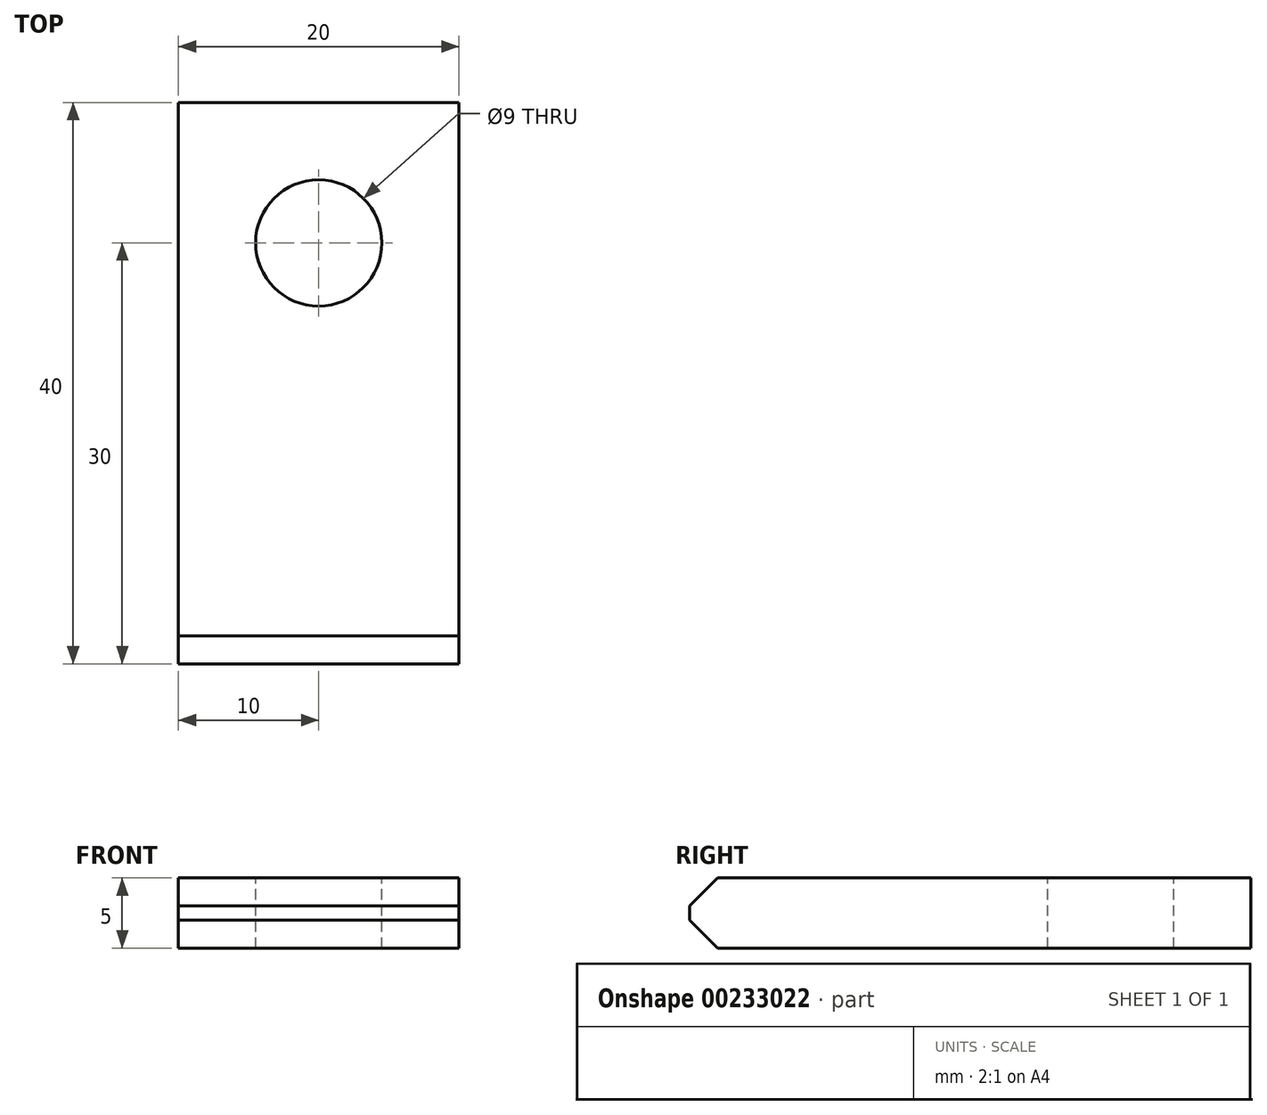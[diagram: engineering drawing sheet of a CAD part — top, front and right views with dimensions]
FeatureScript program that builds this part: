
annotation { "Feature Type Name" : "Feature", "Feature Type Description" : "" }
export const myFeature = defineFeature(function(context is Context, id is Id, definition is map)
    precondition{}
    {
        {
            var Q0;
            Q0=qCreatedBy(makeId("Front.planeOp"),FACE);
            var sketch = newSketch(context, id + "F0", { "sketchPlane" : qUnion([Q0])});
            skLineSegment(sketch, "E0.bottom", {"start": v(10, 2.5) * mm, "end": v(-10, 2.5) * mm});
            skLineSegment(sketch, "E0.top", {"start": v(10, -2.5) * mm, "end": v(-10, -2.5) * mm});
            skLineSegment(sketch, "E0.left", {"start": v(10, 2.5) * mm, "end": v(10, -2.5) * mm});
            skLineSegment(sketch, "E0.right", {"start": v(-10, 2.5) * mm, "end": v(-10, -2.5) * mm});
            skPoint(sketch, "E0.middle", {"position": v(0, 0) * mm});
            skSolve(sketch);
        }
        {
            var Q0;
            Q0=makeQuery(id+"F0.imprint","IMPRINT",FACE,{"disambiguationData":[TD([[makeQuery(id+"F0.imprint","IMPRINT",EDGE,{"derivedFrom":sQuery(id+"F0.wireOp",EDGE,"E0.bottom")}),1.0]])]});
            extrude(context, id + "F1", {"entities" : qUnion([Q0]), "depth" : 40 * mm});
        }
        {
            var Q0;
            Q0=makeQuery(id+"F1.opExtrude","SWEPT_FACE",FACE,{"disambiguationData":[OSD([sQuery(id+"F0.wireOp",EDGE,"E0.bottom")])]});
            var sketch = newSketch(context, id + "F2", { "sketchPlane" : qUnion([Q0])});
            skCircle(sketch, "E1", {"center": v(0, -10) * mm, "radius": 8 * mm, "construction": true});
            skSolve(sketch);
        }
        {
            var Q0;
            Q0=sQuery(id+"F2.wireOp",VERTEX,"E1.center");
            var Q1;
            Q1=makeQuery(id+"F1.opExtrude","SWEPT_BODY",BODY,{"disambiguationData":[OSD([sQuery(id+"F0.wireOp",EDGE,"E0.bottom"),sQuery(id+"F0.wireOp",EDGE,"E0.top"),sQuery(id+"F0.wireOp",EDGE,"E0.left"),sQuery(id+"F0.wireOp",EDGE,"E0.right")])]});
            hole(context, id + "F3", {"style" : HoleStyle.SIMPLE, "endStyle" : HoleEndStyle.THROUGH, "holeDiameter" : 9 * mm, "startFromSketch" : true, "locations" : qUnion([Q0]), "scope" : qUnion([Q1]), "isTappedThrough" : true});
        }
        {
            var Q0;
            Q0=makeQuery(id+"F1.opExtrude","CAP_EDGE",EDGE,{"disambiguationData":[OSD([sQuery(id+"F0.wireOp",EDGE,"E0.bottom")])],"isStart":false});
            var Q1;
            Q1=makeQuery(id+"F1.opExtrude","CAP_EDGE",EDGE,{"disambiguationData":[OSD([sQuery(id+"F0.wireOp",EDGE,"E0.top")])],"isStart":false});
            chamfer(context, id + "F4", {"entities" : qUnion([Q0, Q1]), "width" : 2 * mm, "tangentPropagation" : true});
        }
    });
